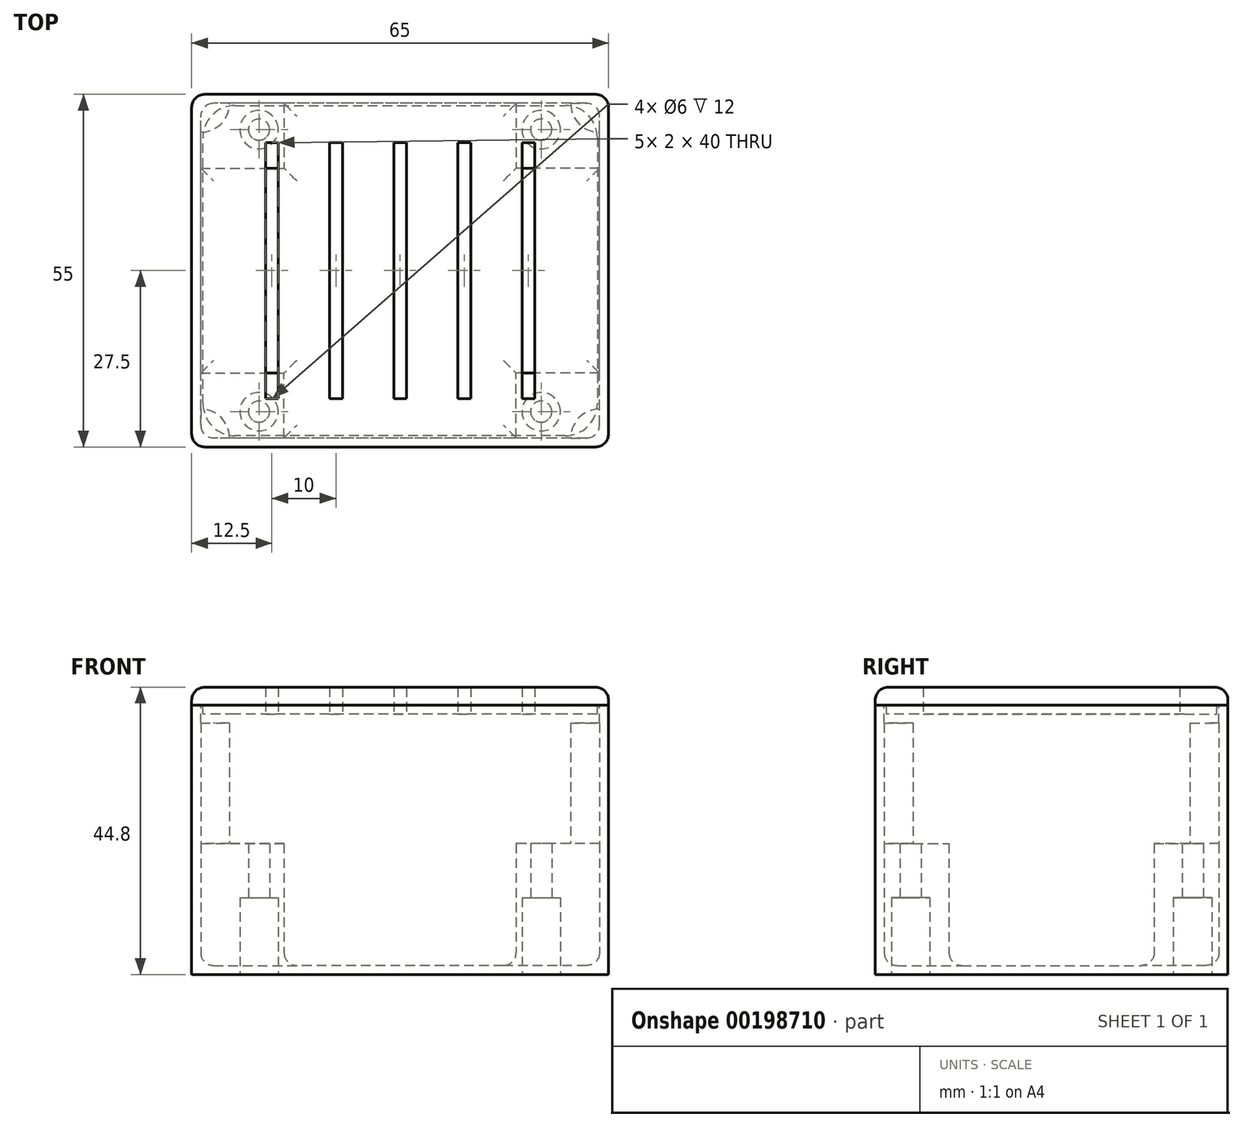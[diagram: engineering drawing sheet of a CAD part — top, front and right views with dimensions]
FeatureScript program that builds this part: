
annotation { "Feature Type Name" : "Feature", "Feature Type Description" : "" }
export const myFeature = defineFeature(function(context is Context, id is Id, definition is map)
    precondition{}
    {
        {
            assignVariable(context, id + "F0", {"name" : "thickness", "anyValue" : 1.4 * mm});
        }
        {
            assignVariable(context, id + "F1", {"name" : "box_height", "anyValue" : 42 * mm});
        }
        {
            assignVariable(context, id + "F2", {"name" : "mount_height", "anyValue" : 19 * mm});
        }
        {
            var Q0;
            Q0=qCreatedBy(makeId("Top.planeOp"),FACE);
            var sketch = newSketch(context, id + "F3", { "sketchPlane" : qUnion([Q0])});
            skLineSegment(sketch, "E0.bottom", {"start": v(32.5, 27.5) * mm, "end": v(-32.5, 27.5) * mm});
            skLineSegment(sketch, "E0.top", {"start": v(32.5, -27.5) * mm, "end": v(-32.5, -27.5) * mm});
            skLineSegment(sketch, "E0.left", {"start": v(32.5, 27.5) * mm, "end": v(32.5, -27.5) * mm});
            skLineSegment(sketch, "E0.right", {"start": v(-32.5, 27.5) * mm, "end": v(-32.5, -27.5) * mm});
            skPoint(sketch, "E0.middle", {"position": v(0, 0) * mm});
            skSolve(sketch);
        }
        {
            var Q0;
            Q0=makeQuery(id+"F3.imprint","IMPRINT",FACE,{"disambiguationData":[TD([[makeQuery(id+"F3.imprint","IMPRINT",EDGE,{"derivedFrom":sQuery(id+"F3.wireOp",EDGE,"E0.bottom")}),1.0]])]});
            extrude(context, id + "F4", {"entities" : qUnion([Q0]), "depth" : getVariable(context, 'box_height')});
        }
        {
            var Q0;
            Q0=makeQuery(id+"F4.opExtrude","CAP_FACE",FACE,{"disambiguationData":[OSD([sQuery(id+"F3.wireOp",EDGE,"E0.bottom"),sQuery(id+"F3.wireOp",EDGE,"E0.top"),sQuery(id+"F3.wireOp",EDGE,"E0.left"),sQuery(id+"F3.wireOp",EDGE,"E0.right")])],"isStart":false});
            var sketch = newSketch(context, id + "F5", { "sketchPlane" : qUnion([Q0])});
            skLineSegment(sketch, "E1.bottom", {"start": v(31.1, -26.1) * mm, "end": v(-31.1, -26.1) * mm});
            skLineSegment(sketch, "E1.top", {"start": v(31.1, 26.1) * mm, "end": v(-31.1, 26.1) * mm});
            skLineSegment(sketch, "E1.left", {"start": v(31.1, -26.1) * mm, "end": v(31.1, 26.1) * mm});
            skLineSegment(sketch, "E1.right", {"start": v(-31.1, -26.1) * mm, "end": v(-31.1, 26.1) * mm});
            skPoint(sketch, "E1.middle", {"position": v(0, 0) * mm});
            skSolve(sketch);
        }
        {
            var Q0;
            Q0=makeQuery(id+"F5.imprint","IMPRINT",FACE,{"disambiguationData":[TD([[makeQuery(id+"F5.imprint","IMPRINT",EDGE,{"derivedFrom":sQuery(id+"F5.wireOp",EDGE,"E1.bottom")}),-1.0]])]});
            extrude(context, id + "F6", {"entities" : qUnion([Q0]), "operationType" : NewBodyOperationType.REMOVE, "oppositeDirection" : true, "depth" : getVariable(context, 'box_height') - getVariable(context, 'thickness')});
        }
        {
            var Q0;
            Q0=makeQuery(id+"F6.boolean.opBoolean","COPY",FACE,{"derivedFrom":makeQuery(id+"F6.opExtrude","CAP_FACE",FACE,{"disambiguationData":[OSD([sQuery(id+"F5.wireOp",EDGE,"E1.bottom"),sQuery(id+"F5.wireOp",EDGE,"E1.top"),sQuery(id+"F5.wireOp",EDGE,"E1.left"),sQuery(id+"F5.wireOp",EDGE,"E1.right")])],"isStart":false})});
            var sketch = newSketch(context, id + "F7", { "sketchPlane" : qUnion([Q0])});
            skLineSegment(sketch, "E2.bottom", {"start": v(31.1, 26.1) * mm, "end": v(18.1, 26.1) * mm});
            skLineSegment(sketch, "E2.top", {"start": v(31.1, 16) * mm, "end": v(18.1, 16) * mm});
            skLineSegment(sketch, "E2.left", {"start": v(31.1, 26.1) * mm, "end": v(31.1, 16) * mm});
            skLineSegment(sketch, "E2.right", {"start": v(18.1, 26.1) * mm, "end": v(18.1, 16) * mm});
            skLineSegment(sketch, "E3.bottom", {"start": v(31.1, -26.1) * mm, "end": v(18.1, -26.1) * mm});
            skLineSegment(sketch, "E3.top", {"start": v(31.1, -16) * mm, "end": v(18.1, -16) * mm});
            skLineSegment(sketch, "E3.left", {"start": v(31.1, -26.1) * mm, "end": v(31.1, -16) * mm});
            skLineSegment(sketch, "E3.right", {"start": v(18.1, -26.1) * mm, "end": v(18.1, -16) * mm});
            skLineSegment(sketch, "E4.bottom", {"start": v(-31.1, -26.1) * mm, "end": v(-18.1, -26.1) * mm});
            skLineSegment(sketch, "E4.top", {"start": v(-31.1, -16) * mm, "end": v(-18.1, -16) * mm});
            skLineSegment(sketch, "E4.left", {"start": v(-31.1, -26.1) * mm, "end": v(-31.1, -16) * mm});
            skLineSegment(sketch, "E4.right", {"start": v(-18.1, -26.1) * mm, "end": v(-18.1, -16) * mm});
            skLineSegment(sketch, "E5.bottom", {"start": v(-31.1, 26.1) * mm, "end": v(-18.1, 26.1) * mm});
            skLineSegment(sketch, "E5.top", {"start": v(-31.1, 16) * mm, "end": v(-18.1, 16) * mm});
            skLineSegment(sketch, "E5.left", {"start": v(-31.1, 26.1) * mm, "end": v(-31.1, 16) * mm});
            skLineSegment(sketch, "E5.right", {"start": v(-18.1, 26.1) * mm, "end": v(-18.1, 16) * mm});
            skPoint(sketch, "E6.middle", {"position": v(0, 0) * mm});
            skSolve(sketch);
        }
        {
            var Q0;
            Q0 = qSketchRegion(id + "F7", true);
            extrude(context, id + "F8", {"entities" : qUnion([Q0]), "operationType" : NewBodyOperationType.ADD, "depth" : getVariable(context, 'mount_height')});
        }
        {
            var Q0;
            Q0=makeQuery(id+"F4.opExtrude","CAP_FACE",FACE,{"disambiguationData":[OSD([sQuery(id+"F3.wireOp",EDGE,"E0.bottom"),sQuery(id+"F3.wireOp",EDGE,"E0.top"),sQuery(id+"F3.wireOp",EDGE,"E0.left"),sQuery(id+"F3.wireOp",EDGE,"E0.right")])],"isStart":true});
            var sketch = newSketch(context, id + "F9", { "sketchPlane" : qUnion([Q0])});
            skLineSegment(sketch, "E7.bottom", {"start": v(22, 22) * mm, "end": v(-22, 22) * mm});
            skLineSegment(sketch, "E7.top", {"start": v(22, -22) * mm, "end": v(-22, -22) * mm});
            skLineSegment(sketch, "E7.left", {"start": v(22, 22) * mm, "end": v(22, -22) * mm});
            skLineSegment(sketch, "E7.right", {"start": v(-22, 22) * mm, "end": v(-22, -22) * mm});
            skPoint(sketch, "E7.middle", {"position": v(0, 0) * mm});
            skSolve(sketch);
        }
        {
            var Q0;
            Q0=sQuery(id+"F9.wireOp",VERTEX,"E7.left.end");
            var Q1;
            Q1=sQuery(id+"F9.wireOp",VERTEX,"E7.right.end");
            var Q2;
            Q2=sQuery(id+"F9.wireOp",VERTEX,"E7.right.start");
            var Q3;
            Q3=sQuery(id+"F9.wireOp",VERTEX,"E7.left.start");
            var Q4;
            Q4=makeQuery(id+"F4.opExtrude","SWEPT_BODY",BODY,{"disambiguationData":[OSD([sQuery(id+"F3.wireOp",EDGE,"E0.bottom"),sQuery(id+"F3.wireOp",EDGE,"E0.top"),sQuery(id+"F3.wireOp",EDGE,"E0.left"),sQuery(id+"F3.wireOp",EDGE,"E0.right")])]});
            hole(context, id + "F10", {"style" : HoleStyle.C_BORE, "endStyle" : HoleEndStyle.THROUGH, "holeDiameter" : 3.3 * mm, "cBoreDiameter" : 6 * mm, "cBoreDepth" : 12 * mm, "startFromSketch" : true, "locations" : qUnion([Q0, Q1, Q2, Q3]), "scope" : qUnion([Q4]), "isTappedThrough" : true});
        }
        {
            var Q0;
            Q0=makeQuery(id+"F6.boolean.opBoolean","COPY",FACE,{"derivedFrom":makeQuery(id+"F6.opExtrude","CAP_FACE",FACE,{"disambiguationData":[OSD([sQuery(id+"F5.wireOp",EDGE,"E1.bottom"),sQuery(id+"F5.wireOp",EDGE,"E1.top"),sQuery(id+"F5.wireOp",EDGE,"E1.left"),sQuery(id+"F5.wireOp",EDGE,"E1.right")])],"isStart":false})});
            fillet(context, id + "F11", {"entities" : qUnion([Q0]), "radius" : 2 * mm, "tangentPropagation" : true, "allowEdgeOverflow" : false});
        }
        {
            var Q0;
            Q0=makeQuery(id+"F6.boolean.opBoolean","COPY",EDGE,{"derivedFrom":makeQuery(id+"F6.opExtrude","SWEPT_EDGE",EDGE,{"disambiguationData":[OSD([sQuery(id+"F5.wireOp",EDGE,"E1.top"),sQuery(id+"F5.wireOp",EDGE,"E1.left")])]})});
            var Q1;
            Q1=makeQuery(id+"F6.boolean.opBoolean","COPY",EDGE,{"derivedFrom":makeQuery(id+"F6.opExtrude","SWEPT_EDGE",EDGE,{"disambiguationData":[OSD([sQuery(id+"F5.wireOp",EDGE,"E1.top"),sQuery(id+"F5.wireOp",EDGE,"E1.right")])]})});
            var Q2;
            Q2=makeQuery(id+"F6.boolean.opBoolean","COPY",EDGE,{"derivedFrom":makeQuery(id+"F6.opExtrude","SWEPT_EDGE",EDGE,{"disambiguationData":[OSD([sQuery(id+"F5.wireOp",EDGE,"E1.bottom"),sQuery(id+"F5.wireOp",EDGE,"E1.right")])]})});
            var Q3;
            Q3=makeQuery(id+"F6.boolean.opBoolean","COPY",EDGE,{"derivedFrom":makeQuery(id+"F6.opExtrude","SWEPT_EDGE",EDGE,{"disambiguationData":[OSD([sQuery(id+"F5.wireOp",EDGE,"E1.bottom"),sQuery(id+"F5.wireOp",EDGE,"E1.left")])]})});
            fillet(context, id + "F12", {"entities" : qUnion([Q0, Q1, Q2, Q3]), "radius" : 2 * mm, "tangentPropagation" : true, "allowEdgeOverflow" : false});
        }
        {
            var Q0;
            Q0=makeQuery(id+"F4.opExtrude","CAP_FACE",FACE,{"disambiguationData":[OSD([sQuery(id+"F3.wireOp",EDGE,"E0.bottom"),sQuery(id+"F3.wireOp",EDGE,"E0.top"),sQuery(id+"F3.wireOp",EDGE,"E0.left"),sQuery(id+"F3.wireOp",EDGE,"E0.right")])],"isStart":false});
            var sketch = newSketch(context, id + "F13", { "sketchPlane" : qUnion([Q0])});
            skLineSegment(sketch, "E8.bottom", {"start": v(-32.5, 27.5) * mm, "end": v(32.5, 27.5) * mm});
            skLineSegment(sketch, "E8.top", {"start": v(-32.5, -27.5) * mm, "end": v(32.5, -27.5) * mm});
            skLineSegment(sketch, "E8.left", {"start": v(-32.5, 27.5) * mm, "end": v(-32.5, -27.5) * mm});
            skLineSegment(sketch, "E8.right", {"start": v(32.5, 27.5) * mm, "end": v(32.5, -27.5) * mm});
            skSolve(sketch);
        }
        {
            var Q0;
            Q0=makeQuery(id+"F4.opExtrude","SWEPT_EDGE",EDGE,{"disambiguationData":[OSD([sQuery(id+"F3.wireOp",EDGE,"E0.top"),sQuery(id+"F3.wireOp",EDGE,"E0.right")])]});
            var Q1;
            Q1=makeQuery(id+"F4.opExtrude","SWEPT_EDGE",EDGE,{"disambiguationData":[OSD([sQuery(id+"F3.wireOp",EDGE,"E0.top"),sQuery(id+"F3.wireOp",EDGE,"E0.left")])]});
            var Q2;
            Q2=makeQuery(id+"F4.opExtrude","SWEPT_EDGE",EDGE,{"disambiguationData":[OSD([sQuery(id+"F3.wireOp",EDGE,"E0.bottom"),sQuery(id+"F3.wireOp",EDGE,"E0.left")])]});
            var Q3;
            Q3=makeQuery(id+"F4.opExtrude","SWEPT_EDGE",EDGE,{"disambiguationData":[OSD([sQuery(id+"F3.wireOp",EDGE,"E0.bottom"),sQuery(id+"F3.wireOp",EDGE,"E0.right")])]});
            fillet(context, id + "F14", {"entities" : qUnion([Q0, Q1, Q2, Q3]), "radius" : 2 * mm, "tangentPropagation" : true, "allowEdgeOverflow" : false});
        }
        {
            var Q0;
            Q0 = qSketchRegion(id + "F13", true);
            extrude(context, id + "F15", {"entities" : qUnion([Q0]), "depth" : getVariable(context, 'thickness') * 2});
        }
        {
            var Q0;
            Q0=makeQuery(id+"F15.opExtrude","SWEPT_EDGE",EDGE,{"disambiguationData":[OSD([sQuery(id+"F13.wireOp",EDGE,"E8.top"),sQuery(id+"F13.wireOp",EDGE,"E8.left")])]});
            var Q1;
            Q1=makeQuery(id+"F15.opExtrude","SWEPT_EDGE",EDGE,{"disambiguationData":[OSD([sQuery(id+"F13.wireOp",EDGE,"E8.top"),sQuery(id+"F13.wireOp",EDGE,"E8.right")])]});
            var Q2;
            Q2=makeQuery(id+"F15.opExtrude","SWEPT_EDGE",EDGE,{"disambiguationData":[OSD([sQuery(id+"F13.wireOp",EDGE,"E8.bottom"),sQuery(id+"F13.wireOp",EDGE,"E8.left")])]});
            var Q3;
            Q3=makeQuery(id+"F15.opExtrude","SWEPT_EDGE",EDGE,{"disambiguationData":[OSD([sQuery(id+"F13.wireOp",EDGE,"E8.bottom"),sQuery(id+"F13.wireOp",EDGE,"E8.right")])]});
            fillet(context, id + "F16", {"entities" : qUnion([Q0, Q1, Q2, Q3]), "radius" : 2 * mm, "tangentPropagation" : true, "allowEdgeOverflow" : false});
        }
        {
            var Q0;
            Q0=makeQuery(id+"F15.opExtrude","CAP_FACE",FACE,{"disambiguationData":[OSD([sQuery(id+"F13.wireOp",EDGE,"E8.bottom"),sQuery(id+"F13.wireOp",EDGE,"E8.top"),sQuery(id+"F13.wireOp",EDGE,"E8.left"),sQuery(id+"F13.wireOp",EDGE,"E8.right")])],"isStart":true});
            var sketch = newSketch(context, id + "F17", { "sketchPlane" : qUnion([Q0])});
            skPoint(sketch, "E9.middle", {"position": v(0, 0) * mm});
            skLineSegment(sketch, "E10.0", {"start": v(30.75, -20.75) * mm, "end": v(30.75, 20.75) * mm});
            skLineSegment(sketch, "E10.1", {"start": v(-25.75, -25.75) * mm, "end": v(25.75, -25.75) * mm});
            skLineSegment(sketch, "E10.2", {"start": v(-30.75, 20.75) * mm, "end": v(-30.75, -20.75) * mm});
            skLineSegment(sketch, "E10.3", {"start": v(25.75, 25.75) * mm, "end": v(-25.75, 25.75) * mm});
            skPoint(sketch, "E11.visualSharp", {"position": v(30.75, -25.75) * mm});
            skArc(sketch, "E11.filletArc", {"start": v(25.75, -25.75) * mm, "mid": v(29.29, -24.29) * mm, "end": v(30.75, -20.75) * mm});
            skPoint(sketch, "E12.visualSharp", {"position": v(30.75, 25.75) * mm});
            skArc(sketch, "E12.filletArc", {"start": v(30.75, 20.75) * mm, "mid": v(29.29, 24.29) * mm, "end": v(25.75, 25.75) * mm});
            skPoint(sketch, "E13.visualSharp", {"position": v(-30.75, 25.75) * mm});
            skArc(sketch, "E13.filletArc", {"start": v(-25.75, 25.75) * mm, "mid": v(-29.29, 24.29) * mm, "end": v(-30.75, 20.75) * mm});
            skPoint(sketch, "E14.visualSharp", {"position": v(-30.75, -25.75) * mm});
            skArc(sketch, "E14.filletArc", {"start": v(-30.75, -20.75) * mm, "mid": v(-29.29, -24.29) * mm, "end": v(-25.75, -25.75) * mm});
            skSolve(sketch);
        }
        {
            var Q0;
            Q0=makeQuery(id+"F17.imprint","IMPRINT",FACE,{"disambiguationData":[TD([[makeQuery(id+"F17.imprint","IMPRINT",EDGE,{"derivedFrom":sQuery(id+"F17.wireOp",EDGE,"E10.0")}),1.0]])]});
            extrude(context, id + "F18", {"entities" : qUnion([Q0]), "operationType" : NewBodyOperationType.ADD, "depth" : getVariable(context, 'thickness')});
        }
        {
            var Q0;
            Q0=makeQuery(id+"F18.opExtrude","CAP_FACE",FACE,{"disambiguationData":[OSD([sQuery(id+"F17.wireOp",EDGE,"E10.0"),sQuery(id+"F17.wireOp",EDGE,"E10.1"),sQuery(id+"F17.wireOp",EDGE,"E10.2"),sQuery(id+"F17.wireOp",EDGE,"E10.3"),sQuery(id+"F17.wireOp",EDGE,"E11.filletArc"),sQuery(id+"F17.wireOp",EDGE,"E12.filletArc"),sQuery(id+"F17.wireOp",EDGE,"E13.filletArc"),sQuery(id+"F17.wireOp",EDGE,"E14.filletArc")])],"isStart":false});
            var sketch = newSketch(context, id + "F19", { "sketchPlane" : qUnion([Q0])});
            skLineSegment(sketch, "E15.bottom", {"start": v(-1, 20) * mm, "end": v(1, 20) * mm});
            skLineSegment(sketch, "E15.top", {"start": v(-1, -20) * mm, "end": v(1, -20) * mm});
            skLineSegment(sketch, "E15.left", {"start": v(-1, 20) * mm, "end": v(-1, -20) * mm});
            skLineSegment(sketch, "E15.right", {"start": v(1, 20) * mm, "end": v(1, -20) * mm});
            skPoint(sketch, "E15.middle", {"position": v(0, 0) * mm});
            skLineSegment(sketch, "E16.1.0.0", {"start": v(-11, 20) * mm, "end": v(-9, 20) * mm});
            skLineSegment(sketch, "E16.1.0.1", {"start": v(-9, 20) * mm, "end": v(-9, -20) * mm});
            skLineSegment(sketch, "E16.1.0.2", {"start": v(-11, 20) * mm, "end": v(-11, -20) * mm});
            skLineSegment(sketch, "E16.1.0.3", {"start": v(-11, -20) * mm, "end": v(-9, -20) * mm});
            skLineSegment(sketch, "E16.2.0.0", {"start": v(-21, 20) * mm, "end": v(-19, 20) * mm});
            skLineSegment(sketch, "E16.2.0.1", {"start": v(-19, 20) * mm, "end": v(-19, -20) * mm});
            skLineSegment(sketch, "E16.2.0.2", {"start": v(-21, 20) * mm, "end": v(-21, -20) * mm});
            skLineSegment(sketch, "E16.2.0.3", {"start": v(-21, -20) * mm, "end": v(-19, -20) * mm});
            skLineSegment(sketch, "E16.direction1", {"start": v(-1, 20) * mm, "end": v(-11, 20) * mm, "construction": true});
            skLineSegment(sketch, "E17.1.0.0", {"start": v(9, 20) * mm, "end": v(11, 20) * mm});
            skLineSegment(sketch, "E17.1.0.1", {"start": v(9, 20) * mm, "end": v(9, -20) * mm});
            skLineSegment(sketch, "E17.1.0.2", {"start": v(11, 20) * mm, "end": v(11, -20) * mm});
            skLineSegment(sketch, "E17.1.0.3", {"start": v(9, -20) * mm, "end": v(11, -20) * mm});
            skLineSegment(sketch, "E17.2.0.0", {"start": v(19, 20) * mm, "end": v(21, 20) * mm});
            skLineSegment(sketch, "E17.2.0.1", {"start": v(19, 20) * mm, "end": v(19, -20) * mm});
            skLineSegment(sketch, "E17.2.0.2", {"start": v(21, 20) * mm, "end": v(21, -20) * mm});
            skLineSegment(sketch, "E17.2.0.3", {"start": v(19, -20) * mm, "end": v(21, -20) * mm});
            skLineSegment(sketch, "E17.direction1", {"start": v(-1, 20) * mm, "end": v(9, 20) * mm, "construction": true});
            skSolve(sketch);
        }
        {
            var Q0;
            Q0 = qSketchRegion(id + "F19", true);
            extrude(context, id + "F20", {"entities" : qUnion([Q0]), "operationType" : NewBodyOperationType.REMOVE, "endBound" : BoundingType.THROUGH_ALL, "oppositeDirection" : true, "depth" : 25 * mm});
        }
        {
            var Q0;
            Q0=makeQuery(id+"F15.opExtrude","CAP_EDGE",EDGE,{"disambiguationData":[OSD([sQuery(id+"F13.wireOp",EDGE,"E8.right")])],"isStart":false});
            var Q1;
            Q1=makeQuery(id+"F15.opExtrude","CAP_EDGE",EDGE,{"disambiguationData":[OSD([sQuery(id+"F13.wireOp",EDGE,"E8.bottom")])],"isStart":false});
            var Q2;
            Q2=makeQuery(id+"F15.opExtrude","CAP_EDGE",EDGE,{"disambiguationData":[OSD([sQuery(id+"F13.wireOp",EDGE,"E8.left")])],"isStart":false});
            var Q3;
            Q3=makeQuery(id+"F15.opExtrude","CAP_EDGE",EDGE,{"disambiguationData":[OSD([sQuery(id+"F13.wireOp",EDGE,"E8.top")])],"isStart":false});
            fillet(context, id + "F21", {"entities" : qUnion([Q0, Q1, Q2, Q3]), "radius" : 2 * mm, "tangentPropagation" : true, "allowEdgeOverflow" : false});
        }
        {
            var Q0;
            Q0=makeQuery(id+"F8.opExtrude","CAP_FACE",FACE,{"disambiguationData":[OSD([sQuery(id+"F7.wireOp",EDGE,"E5.bottom"),sQuery(id+"F7.wireOp",EDGE,"E5.top"),sQuery(id+"F7.wireOp",EDGE,"E5.left"),sQuery(id+"F7.wireOp",EDGE,"E5.right")])],"isStart":false});
            var sketch = newSketch(context, id + "F22", { "sketchPlane" : qUnion([Q0])});
            skLineSegment(sketch, "E18.left", {"start": v(31.1, -26.1) * mm, "end": v(31.1, -21.6) * mm});
            skPoint(sketch, "E19.first.point", {"position": v(-31.1, 21.6) * mm});
            skArc(sketch, "E20", {"start": v(-31.1, 21.6) * mm, "mid": v(-27.92, 22.92) * mm, "end": v(-26.6, 26.1) * mm});
            skLineSegment(sketch, "E21", {"start": v(39.47, 26.1) * mm, "end": v(-35.02, 26.1) * mm, "construction": true});
            skLineSegment(sketch, "E22", {"start": v(31.1, 28.88) * mm, "end": v(31.1, -27.98) * mm, "construction": true});
            skPoint(sketch, "E22.startSnap0", {"position": v(31.1, 24.1) * mm});
            skLineSegment(sketch, "E23", {"start": v(31.1, -27.98) * mm, "end": v(33.37, -26.1) * mm, "construction": true});
            skLineSegment(sketch, "E24", {"start": v(33.37, -26.1) * mm, "end": v(-33.46, -26.1) * mm, "construction": true});
            skLineSegment(sketch, "E25", {"start": v(-31.1, -28.14) * mm, "end": v(-31.1, 29.77) * mm, "construction": true});
            skPoint(sketch, "E25.startSnap0", {"position": v(-31.1, -24.1) * mm});
            skArc(sketch, "E26", {"start": v(-31.1, -21.6) * mm, "mid": v(-27.92, -22.92) * mm, "end": v(-26.6, -26.1) * mm});
            skArc(sketch, "E27", {"start": v(31.1, -21.6) * mm, "mid": v(27.92, -22.92) * mm, "end": v(26.6, -26.1) * mm});
            skArc(sketch, "E28", {"start": v(31.1, 21.6) * mm, "mid": v(27.92, 22.92) * mm, "end": v(26.6, 26.1) * mm});
            skLineSegment(sketch, "E29", {"start": v(-31.1, -21.6) * mm, "end": v(-31.1, -26.1) * mm});
            skLineSegment(sketch, "E30", {"start": v(-26.6, 26.1) * mm, "end": v(-31.1, 26.1) * mm});
            skLineSegment(sketch, "E31", {"start": v(-31.1, 21.6) * mm, "end": v(-31.1, 26.1) * mm});
            skLineSegment(sketch, "E32", {"start": v(26.6, 26.1) * mm, "end": v(31.1, 26.1) * mm});
            skLineSegment(sketch, "E33", {"start": v(26.6, -26.1) * mm, "end": v(31.1, -26.1) * mm});
            skLineSegment(sketch, "E34", {"start": v(-26.6, -26.1) * mm, "end": v(-31.1, -26.1) * mm});
            skLineSegment(sketch, "E35", {"start": v(31.1, 21.6) * mm, "end": v(31.1, 26.1) * mm});
            skSolve(sketch);
        }
        {
            var Q0;
            Q0 = qSketchRegion(id + "F22", true);
            extrude(context, id + "F23", {"entities" : qUnion([Q0]), "operationType" : NewBodyOperationType.ADD, "depth" : getVariable(context, 'box_height') - getVariable(context, 'mount_height') - 3 * getVariable(context, 'thickness')});
        }
    });
